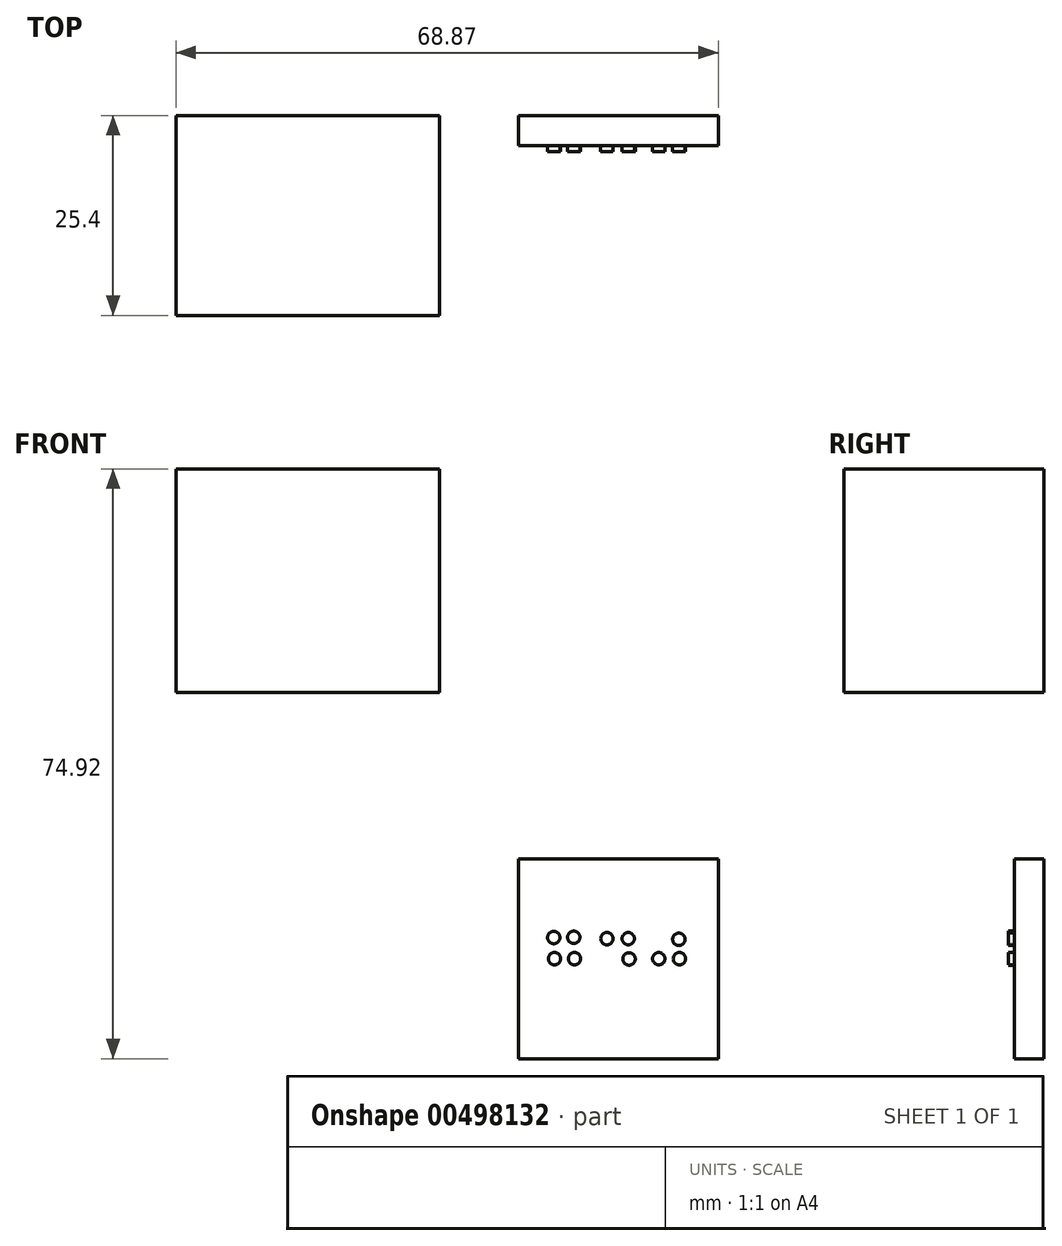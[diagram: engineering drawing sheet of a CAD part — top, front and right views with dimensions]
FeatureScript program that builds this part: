
annotation { "Feature Type Name" : "Feature", "Feature Type Description" : "" }
export const myFeature = defineFeature(function(context is Context, id is Id, definition is map)
    precondition{}
    {
        {
            var Q0;
            Q0=qCreatedBy(makeId("Front.planeOp"),FACE);
            var sketch = newSketch(context, id + "F0", { "sketchPlane" : qUnion([Q0])});
            skLineSegment(sketch, "E0.bottom", {"start": v(12.7, -12.7) * mm, "end": v(-12.7, -12.7) * mm});
            skLineSegment(sketch, "E0.top", {"start": v(12.7, 12.7) * mm, "end": v(-12.7, 12.7) * mm});
            skLineSegment(sketch, "E0.left", {"start": v(12.7, -12.7) * mm, "end": v(12.7, 12.7) * mm});
            skLineSegment(sketch, "E0.right", {"start": v(-12.7, -12.7) * mm, "end": v(-12.7, 12.7) * mm});
            skPoint(sketch, "E0.middle", {"position": v(0, 0) * mm});
            skSolve(sketch);
        }
        {
            var Q0;
            Q0=makeQuery(id+"F0.imprint","IMPRINT",FACE,{"disambiguationData":[TD([[makeQuery(id+"F0.imprint","IMPRINT",EDGE,{"derivedFrom":sQuery(id+"F0.wireOp",EDGE,"E0.bottom")}),-1.0]])]});
            extrude(context, id + "F1", {"entities" : qUnion([Q0]), "depth" : 3.8 * mm});
        }
        {
            var Q0;
            Q0=makeQuery(id+"F1.opExtrude","CAP_FACE",FACE,{"disambiguationData":[OSD([sQuery(id+"F0.wireOp",EDGE,"E0.bottom"),sQuery(id+"F0.wireOp",EDGE,"E0.top"),sQuery(id+"F0.wireOp",EDGE,"E0.left"),sQuery(id+"F0.wireOp",EDGE,"E0.right")])],"isStart":false});
            var sketch = newSketch(context, id + "F2", { "sketchPlane" : qUnion([Q0])});
            skLineSegment(sketch, "E1.bottom", {"start": v(-4.18, 3.81) * mm, "end": v(-9.26, 3.81) * mm});
            skLineSegment(sketch, "E1.top", {"start": v(-4.18, -3.8) * mm, "end": v(-9.26, -3.8) * mm});
            skLineSegment(sketch, "E1.left", {"start": v(-4.18, 3.81) * mm, "end": v(-4.18, -3.8) * mm});
            skLineSegment(sketch, "E1.right", {"start": v(-9.26, 3.81) * mm, "end": v(-9.26, -3.8) * mm});
            skPoint(sketch, "E1.middle", {"position": v(-6.72, 0) * mm});
            skLineSegment(sketch, "E2.bottom", {"start": v(2.54, 3.81) * mm, "end": v(-2.54, 3.81) * mm});
            skLineSegment(sketch, "E2.top", {"start": v(2.54, -3.81) * mm, "end": v(-2.54, -3.81) * mm});
            skLineSegment(sketch, "E2.left", {"start": v(2.54, 3.81) * mm, "end": v(2.54, -3.8) * mm});
            skLineSegment(sketch, "E2.right", {"start": v(-2.54, 3.81) * mm, "end": v(-2.54, -3.81) * mm});
            skPoint(sketch, "E2.middle", {"position": v(0, 0) * mm});
            skLineSegment(sketch, "E3.bottom", {"start": v(9.04, 3.81) * mm, "end": v(3.96, 3.8) * mm});
            skLineSegment(sketch, "E3.top", {"start": v(9.04, -3.8) * mm, "end": v(3.96, -3.81) * mm});
            skLineSegment(sketch, "E3.left", {"start": v(9.04, 3.81) * mm, "end": v(9.04, -3.8) * mm});
            skLineSegment(sketch, "E3.right", {"start": v(3.96, 3.8) * mm, "end": v(3.96, -3.81) * mm});
            skPoint(sketch, "E3.middle", {"position": v(6.5, 0) * mm});
            skSolve(sketch);
        }
        {
            var Q0;
            Q0=makeQuery(id+"F2.imprint","IMPRINT",FACE,{"disambiguationData":[TD([[makeQuery(id+"F2.imprint","IMPRINT",EDGE,{"derivedFrom":sQuery(id+"F2.wireOp",EDGE,"E1.bottom")}),1.0]])]});
            var sketch = newSketch(context, id + "F3", { "sketchPlane" : qUnion([Q0])});
            skCircle(sketch, "E4", {"center": v(-5.56, 0) * mm, "radius": 0.79 * mm});
            skCircle(sketch, "E5", {"center": v(-8.1, 0) * mm, "radius": 0.79 * mm});
            skCircle(sketch, "E6", {"center": v(-8.2, 2.69) * mm, "radius": 0.79 * mm});
            skCircle(sketch, "E7", {"center": v(-5.65, 2.72) * mm, "radius": 0.79 * mm});
            skSolve(sketch);
        }
        {
            var Q0;
            Q0=makeQuery(id+"F2.imprint","IMPRINT",FACE,{"disambiguationData":[TD([[makeQuery(id+"F2.imprint","IMPRINT",EDGE,{"derivedFrom":sQuery(id+"F2.wireOp",EDGE,"E2.bottom")}),1.0]])]});
            var sketch = newSketch(context, id + "F4", { "sketchPlane" : qUnion([Q0])});
            skCircle(sketch, "E8", {"center": v(1.38, -0.04) * mm, "radius": 0.79 * mm});
            skCircle(sketch, "E9", {"center": v(-1.44, 2.55) * mm, "radius": 0.79 * mm});
            skCircle(sketch, "E10", {"center": v(1.26, 2.55) * mm, "radius": 0.79 * mm});
            skSolve(sketch);
        }
        {
            var Q0;
            Q0=makeQuery(id+"F2.imprint","IMPRINT",FACE,{"disambiguationData":[TD([[makeQuery(id+"F2.imprint","IMPRINT",EDGE,{"derivedFrom":sQuery(id+"F2.wireOp",EDGE,"E3.bottom")}),1.0]])]});
            var sketch = newSketch(context, id + "F5", { "sketchPlane" : qUnion([Q0])});
            skCircle(sketch, "E11", {"center": v(7.7, 2.47) * mm, "radius": 0.79 * mm});
            skCircle(sketch, "E12", {"center": v(5.15, 0) * mm, "radius": 0.79 * mm});
            skCircle(sketch, "E13", {"center": v(7.77, 0) * mm, "radius": 0.79 * mm});
            skSolve(sketch);
        }
        {
            var Q0;
            Q0 = qSketchRegion(id + "F3", true);
            var Q1;
            Q1 = qSketchRegion(id + "F5", true);
            var Q2;
            Q2 = qSketchRegion(id + "F4", true);
            extrude(context, id + "F6", {"entities" : qUnion([Q0, Q1, Q2]), "operationType" : NewBodyOperationType.ADD, "depth" : 0.76 * mm, "offsetDistance" : 25.4 * mm});
        }
        {
            var Q0;
            Q0=qCreatedBy(makeId("Front.planeOp"),FACE);
            var sketch = newSketch(context, id + "F7", { "sketchPlane" : qUnion([Q0])});
            skLineSegment(sketch, "E14.bottom", {"start": v(-56.17, 62.22) * mm, "end": v(-22.68, 62.22) * mm});
            skLineSegment(sketch, "E14.top", {"start": v(-56.17, 33.84) * mm, "end": v(-22.68, 33.84) * mm});
            skLineSegment(sketch, "E14.left", {"start": v(-56.17, 62.22) * mm, "end": v(-56.17, 33.84) * mm});
            skLineSegment(sketch, "E14.right", {"start": v(-22.68, 62.22) * mm, "end": v(-22.68, 33.84) * mm});
            skSolve(sketch);
        }
        {
            var Q0;
            Q0 = qSketchRegion(id + "F7", true);
            extrude(context, id + "F8", {"entities" : qUnion([Q0]), "depth" : 25.4 * mm, "offsetDistance" : 25.4 * mm});
        }
    });
